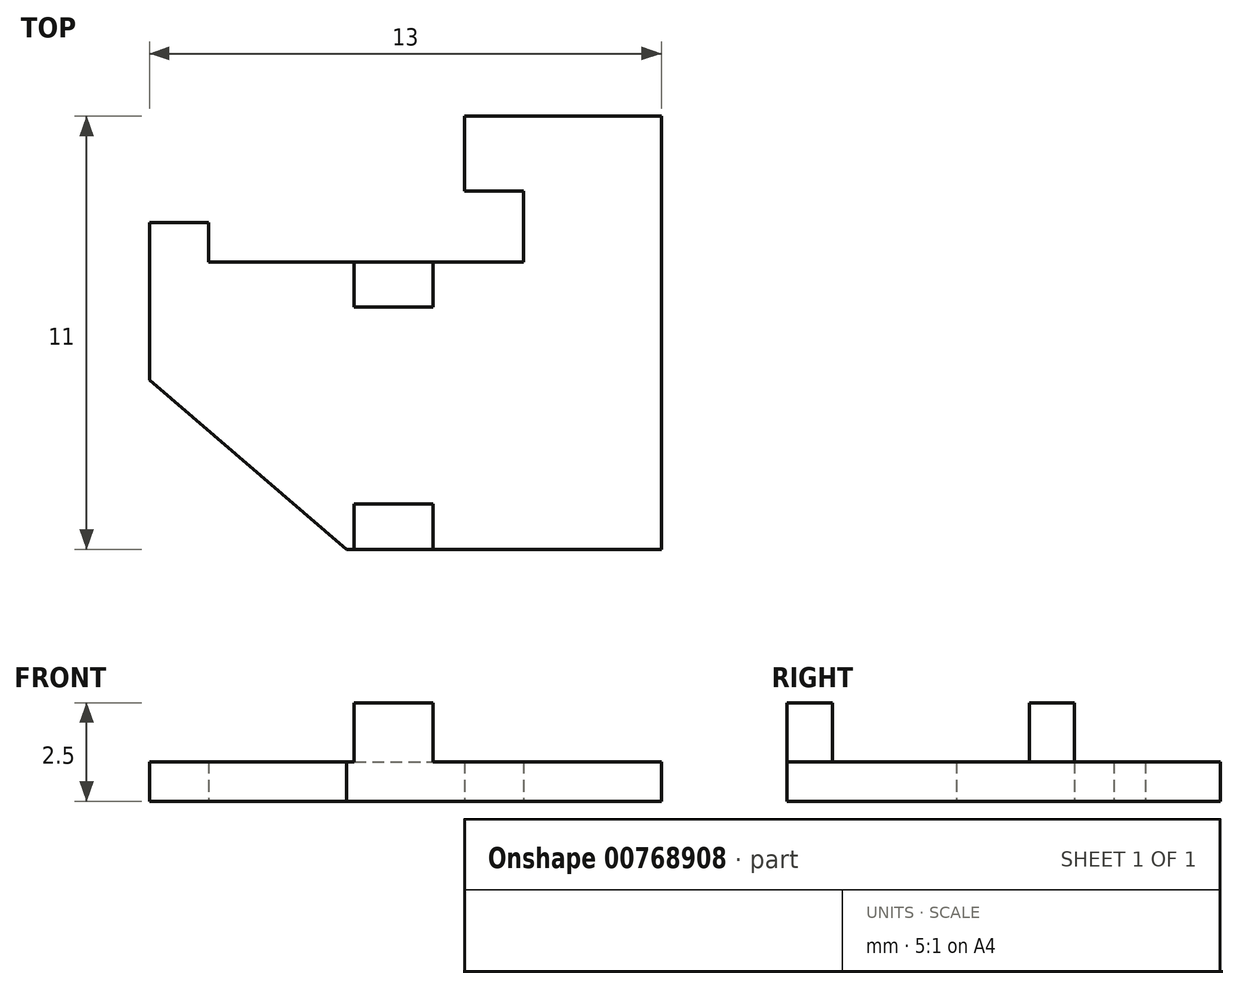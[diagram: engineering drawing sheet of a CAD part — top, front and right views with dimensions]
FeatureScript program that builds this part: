
annotation { "Feature Type Name" : "Feature", "Feature Type Description" : "" }
export const myFeature = defineFeature(function(context is Context, id is Id, definition is map)
    precondition{}
    {
        {
            var Q0;
            Q0=qCreatedBy(makeId("Top.planeOp"),FACE);
            var sketch = newSketch(context, id + "F0", { "sketchPlane" : qUnion([Q0])});
            skLineSegment(sketch, "E0", {"start": v(0, 0) * mm, "end": v(0, 11) * mm});
            skLineSegment(sketch, "E1", {"start": v(0, 11) * mm, "end": v(-5, 11) * mm});
            skLineSegment(sketch, "E2", {"start": v(-5, 11) * mm, "end": v(-5, 9.1) * mm});
            skLineSegment(sketch, "E3", {"start": v(-5, 9.1) * mm, "end": v(-3.5, 9.1) * mm});
            skLineSegment(sketch, "E4", {"start": v(-3.5, 9.1) * mm, "end": v(-3.5, 7.3) * mm});
            skLineSegment(sketch, "E5", {"start": v(-3.5, 7.3) * mm, "end": v(-11.5, 7.3) * mm});
            skLineSegment(sketch, "E6", {"start": v(-11.5, 7.3) * mm, "end": v(-11.5, 8.3) * mm});
            skLineSegment(sketch, "E7", {"start": v(-11.5, 8.3) * mm, "end": v(-13, 8.3) * mm});
            skLineSegment(sketch, "E8", {"start": v(-13, 8.3) * mm, "end": v(-13, 4.3) * mm});
            skLineSegment(sketch, "E9", {"start": v(-13, 4.3) * mm, "end": v(-8, 0) * mm});
            skLineSegment(sketch, "E10", {"start": v(-8, 0) * mm, "end": v(0, 0) * mm});
            skSolve(sketch);
        }
        {
            var Q0;
            Q0 = qSketchRegion(id + "F0", true);
            extrude(context, id + "F1", {"entities" : qUnion([Q0]), "depth" : 1 * mm, "offsetDistance" : 25 * mm});
        }
        {
            var Q0;
            Q0=makeQuery(id+"F1.opExtrude","CAP_FACE",FACE,{"disambiguationData":[OSD([sQuery(id+"F0.wireOp",EDGE,"E0"),sQuery(id+"F0.wireOp",EDGE,"E1"),sQuery(id+"F0.wireOp",EDGE,"E2"),sQuery(id+"F0.wireOp",EDGE,"E3"),sQuery(id+"F0.wireOp",EDGE,"E4"),sQuery(id+"F0.wireOp",EDGE,"E5"),sQuery(id+"F0.wireOp",EDGE,"E6"),sQuery(id+"F0.wireOp",EDGE,"E7"),sQuery(id+"F0.wireOp",EDGE,"E8"),sQuery(id+"F0.wireOp",EDGE,"E9"),sQuery(id+"F0.wireOp",EDGE,"E10")])],"isStart":false});
            var sketch = newSketch(context, id + "F2", { "sketchPlane" : qUnion([Q0])});
            skLineSegment(sketch, "E11.bottom", {"start": v(-5.8, 0) * mm, "end": v(-7.8, 0) * mm});
            skLineSegment(sketch, "E11.top", {"start": v(-5.8, 1.15) * mm, "end": v(-7.8, 1.15) * mm});
            skLineSegment(sketch, "E11.left", {"start": v(-5.8, 0) * mm, "end": v(-5.8, 1.15) * mm});
            skLineSegment(sketch, "E11.right", {"start": v(-7.8, 0) * mm, "end": v(-7.8, 1.15) * mm});
            skLineSegment(sketch, "E12.bottom", {"start": v(-7.8, 7.3) * mm, "end": v(-5.8, 7.3) * mm});
            skLineSegment(sketch, "E12.top", {"start": v(-7.8, 6.15) * mm, "end": v(-5.8, 6.15) * mm});
            skLineSegment(sketch, "E12.left", {"start": v(-7.8, 7.3) * mm, "end": v(-7.8, 6.15) * mm});
            skLineSegment(sketch, "E12.right", {"start": v(-5.8, 7.3) * mm, "end": v(-5.8, 6.15) * mm});
            skLineSegment(sketch, "E13", {"start": v(-5.8, 1.15) * mm, "end": v(-5.8, 6.15) * mm, "construction": true});
            skSolve(sketch);
        }
        {
            var Q0;
            Q0 = qSketchRegion(id + "F2", true);
            extrude(context, id + "F3", {"entities" : qUnion([Q0]), "operationType" : NewBodyOperationType.ADD, "depth" : 1.5 * mm, "offsetDistance" : 25 * mm});
        }
    });
